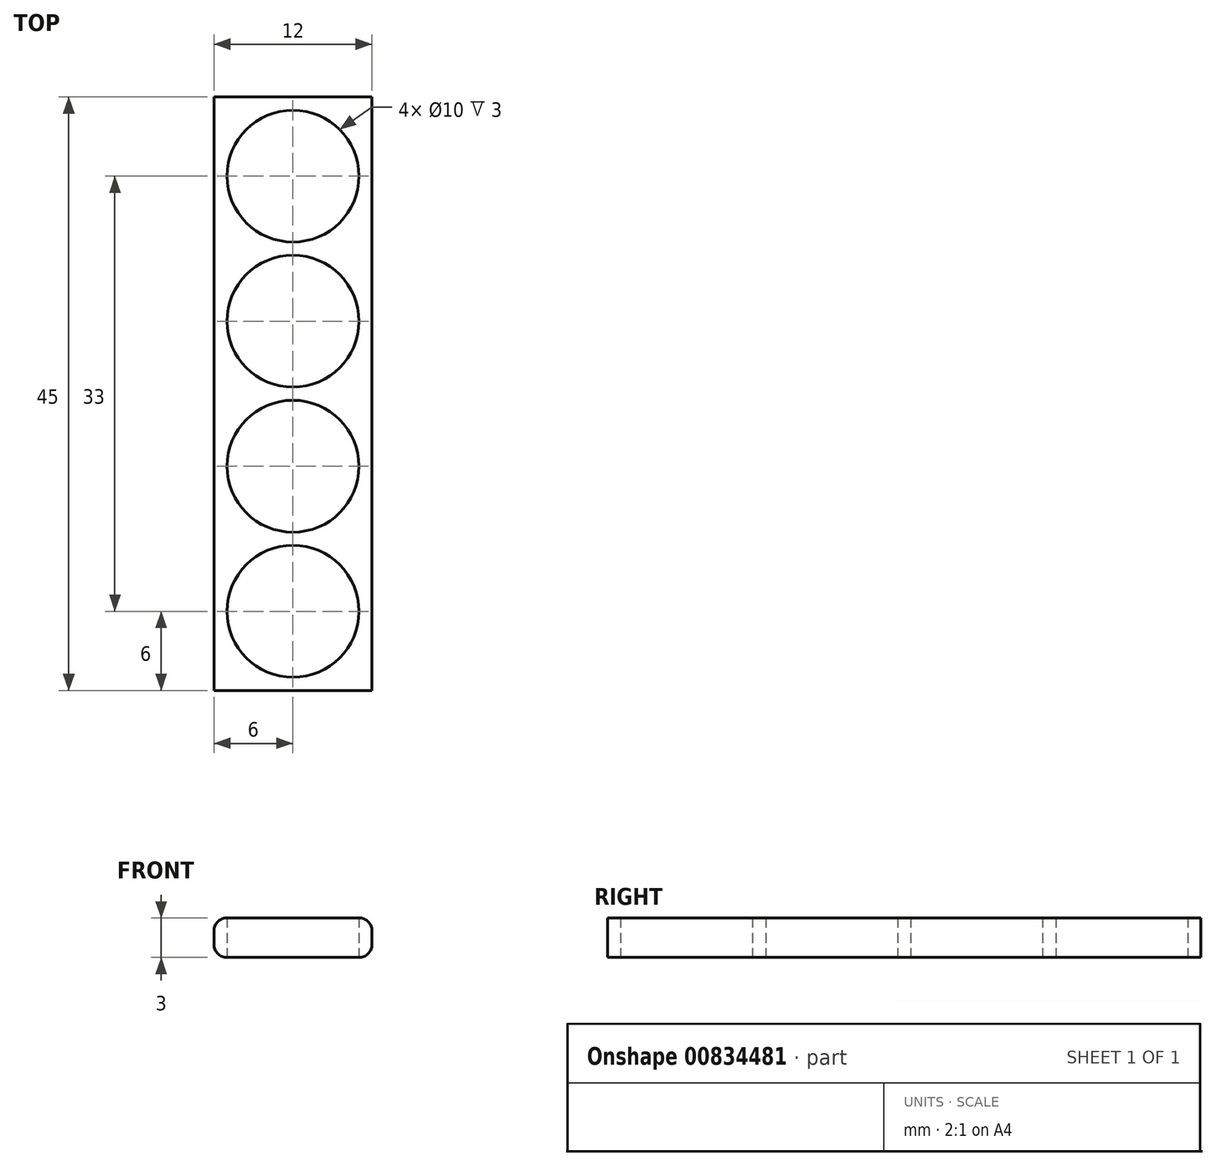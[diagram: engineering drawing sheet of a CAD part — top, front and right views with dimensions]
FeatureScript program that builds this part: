
annotation { "Feature Type Name" : "Feature", "Feature Type Description" : "" }
export const myFeature = defineFeature(function(context is Context, id is Id, definition is map)
    precondition{}
    {
        {
            var Q0;
            Q0=qCreatedBy(makeId("Top.planeOp"),FACE);
            var sketch = newSketch(context, id + "F0", { "sketchPlane" : qUnion([Q0])});
            skLineSegment(sketch, "E0.bottom", {"start": v(0, 0) * mm, "end": v(12, 0) * mm});
            skLineSegment(sketch, "E0.top", {"start": v(0, 45) * mm, "end": v(12, 45) * mm});
            skLineSegment(sketch, "E0.left", {"start": v(0, 0) * mm, "end": v(0, 45) * mm});
            skLineSegment(sketch, "E0.right", {"start": v(12, 0) * mm, "end": v(12, 45) * mm});
            skLineSegment(sketch, "E1", {"start": v(6, 45) * mm, "end": v(6, 0) * mm, "construction": true});
            skCircle(sketch, "E2", {"center": v(6, 39) * mm, "radius": 5 * mm});
            skCircle(sketch, "E3", {"center": v(6, 28) * mm, "radius": 5 * mm});
            skCircle(sketch, "E4", {"center": v(6, 17) * mm, "radius": 5 * mm});
            skCircle(sketch, "E5", {"center": v(6, 6) * mm, "radius": 5 * mm});
            skPoint(sketch, "E6", {"position": v(6, 33.5) * mm});
            skPoint(sketch, "E7", {"position": v(6, 22.5) * mm});
            skPoint(sketch, "E8", {"position": v(6, 11.5) * mm});
            skSolve(sketch);
        }
        {
            var Q0;
            Q0=makeQuery(id+"F0.imprint","IMPRINT",FACE,{"disambiguationData":[TD([[makeQuery(id+"F0.imprint","IMPRINT",EDGE,{"derivedFrom":sQuery(id+"F0.wireOp",EDGE,"E0.bottom")}),1.0]])]});
            extrude(context, id + "F1", {"entities" : qUnion([Q0]), "depth" : 3 * mm, "offsetDistance" : 25 * mm});
        }
        {
            var Q0;
            Q0=makeQuery(id+"F1.opExtrude","CAP_EDGE",EDGE,{"disambiguationData":[OSD([sQuery(id+"F0.wireOp",EDGE,"E0.right")])],"isStart":false});
            var Q1;
            Q1=makeQuery(id+"F1.opExtrude","CAP_EDGE",EDGE,{"disambiguationData":[OSD([sQuery(id+"F0.wireOp",EDGE,"E0.right")])],"isStart":true});
            var Q2;
            Q2=makeQuery(id+"F1.opExtrude","CAP_EDGE",EDGE,{"disambiguationData":[OSD([sQuery(id+"F0.wireOp",EDGE,"E0.left")])],"isStart":false});
            var Q3;
            Q3=makeQuery(id+"F1.opExtrude","CAP_EDGE",EDGE,{"disambiguationData":[OSD([sQuery(id+"F0.wireOp",EDGE,"E0.left")])],"isStart":true});
            fillet(context, id + "F2", {"entities" : qUnion([Q0, Q1, Q2, Q3]), "radius" : 1 * mm, "tangentPropagation" : true, "allowEdgeOverflow" : false});
        }
    });
